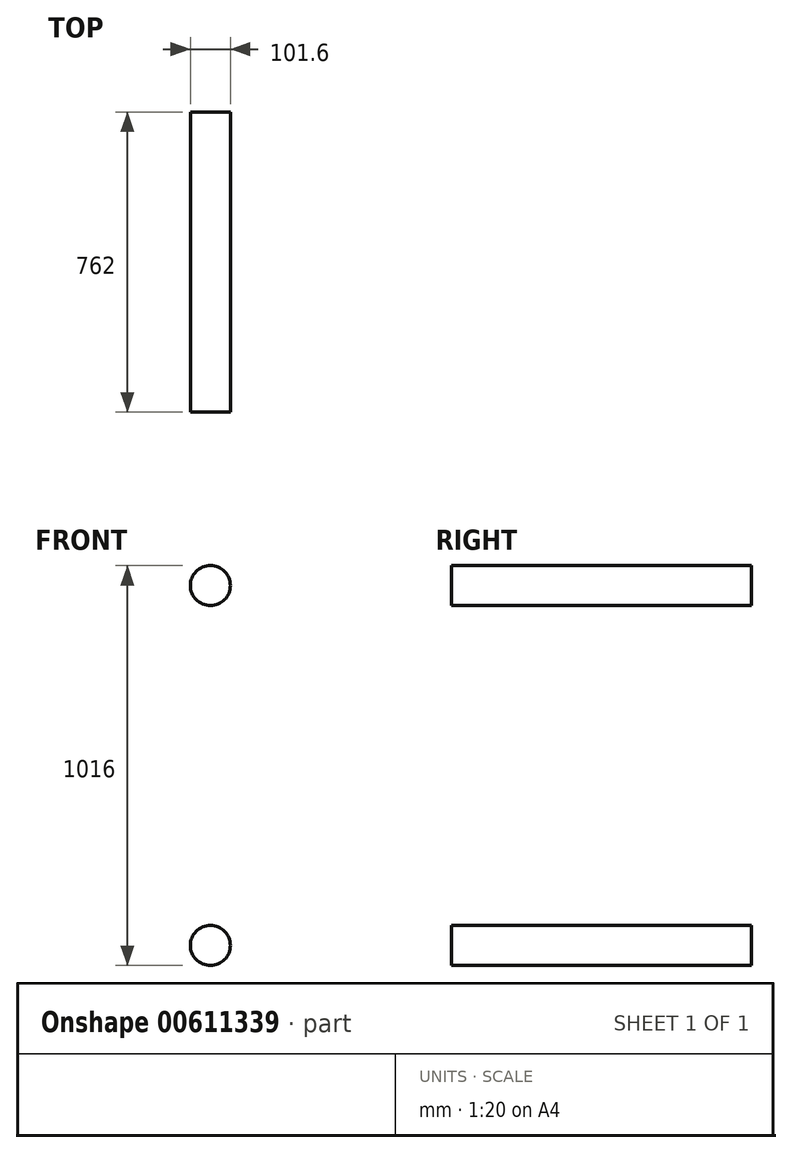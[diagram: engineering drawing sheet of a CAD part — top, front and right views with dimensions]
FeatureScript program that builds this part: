
annotation { "Feature Type Name" : "Feature", "Feature Type Description" : "" }
export const myFeature = defineFeature(function(context is Context, id is Id, definition is map)
    precondition{}
    {
        {
            var Q0;
            Q0=qCreatedBy(makeId("Front.planeOp"),FACE);
            var sketch = newSketch(context, id + "F0", { "sketchPlane" : qUnion([Q0])});
            skLineSegment(sketch, "E0.bottom", {"start": v(-559.4, 407.78) * mm, "end": v(355, 407.78) * mm});
            skLineSegment(sketch, "E0.top", {"start": v(-559.4, 509.38) * mm, "end": v(355, 509.38) * mm});
            skLineSegment(sketch, "E0.left", {"start": v(-559.4, 407.78) * mm, "end": v(-559.4, 509.38) * mm});
            skLineSegment(sketch, "E0.right", {"start": v(355, 407.78) * mm, "end": v(355, 509.38) * mm});
            skLineSegment(sketch, "E1.bottom", {"start": v(-559.4, 509.38) * mm, "end": v(-661, 509.38) * mm});
            skLineSegment(sketch, "E1.top", {"start": v(-559.4, -506.62) * mm, "end": v(-661, -506.62) * mm});
            skLineSegment(sketch, "E1.left", {"start": v(-559.4, 509.38) * mm, "end": v(-559.4, -506.62) * mm});
            skLineSegment(sketch, "E1.right", {"start": v(-661, 509.38) * mm, "end": v(-661, -506.62) * mm});
            skLineSegment(sketch, "E2.bottom", {"start": v(-559.4, -404.99) * mm, "end": v(355, -404.99) * mm});
            skLineSegment(sketch, "E2.top", {"start": v(-559.4, -506.59) * mm, "end": v(355, -506.59) * mm});
            skLineSegment(sketch, "E2.left", {"start": v(-559.4, -404.99) * mm, "end": v(-559.4, -506.59) * mm});
            skLineSegment(sketch, "E2.right", {"start": v(355, -404.99) * mm, "end": v(355, -506.59) * mm});
            skCircle(sketch, "E3", {"center": v(-610.2, 458.58) * mm, "radius": 50.8 * mm});
            skCircle(sketch, "E4", {"center": v(-610.2, -455.82) * mm, "radius": 50.8 * mm});
            skSolve(sketch);
        }
        {
            var Q0;
            {var subQ0=sQuery(id+"F0.wireOp",EDGE,"E3");var subQ1=makeQuery(id+"F0.imprint","INTERSECT",VERTEX,{"derivedFrom":[sQuery(id+"F0.wireOp",EDGE,"E1.bottom"),subQ0]});Q0=makeQuery(id+"F0.imprint","IMPRINT",FACE,{"disambiguationData":[TD([[makeQuery(id+"F0.imprint","IMPRINT",EDGE,{"disambiguationData":[TD([[subQ1,1.0]])],"derivedFrom":subQ0}),1.0]])]});}
            var Q1;
            {var subQ0=sQuery(id+"F0.wireOp",EDGE,"E4");var subQ1=makeQuery(id+"F0.imprint","INTERSECT",VERTEX,{"derivedFrom":[sQuery(id+"F0.wireOp",EDGE,"E1.right"),subQ0]});Q1=makeQuery(id+"F0.imprint","IMPRINT",FACE,{"disambiguationData":[TD([[makeQuery(id+"F0.imprint","IMPRINT",EDGE,{"disambiguationData":[TD([[subQ1,1.0]])],"derivedFrom":subQ0}),1.0]])]});}
            extrude(context, id + "F1", {"entities" : qUnion([Q0, Q1]), "depth" : 762 * mm, "offsetDistance" : 25.4 * mm});
        }
    });
